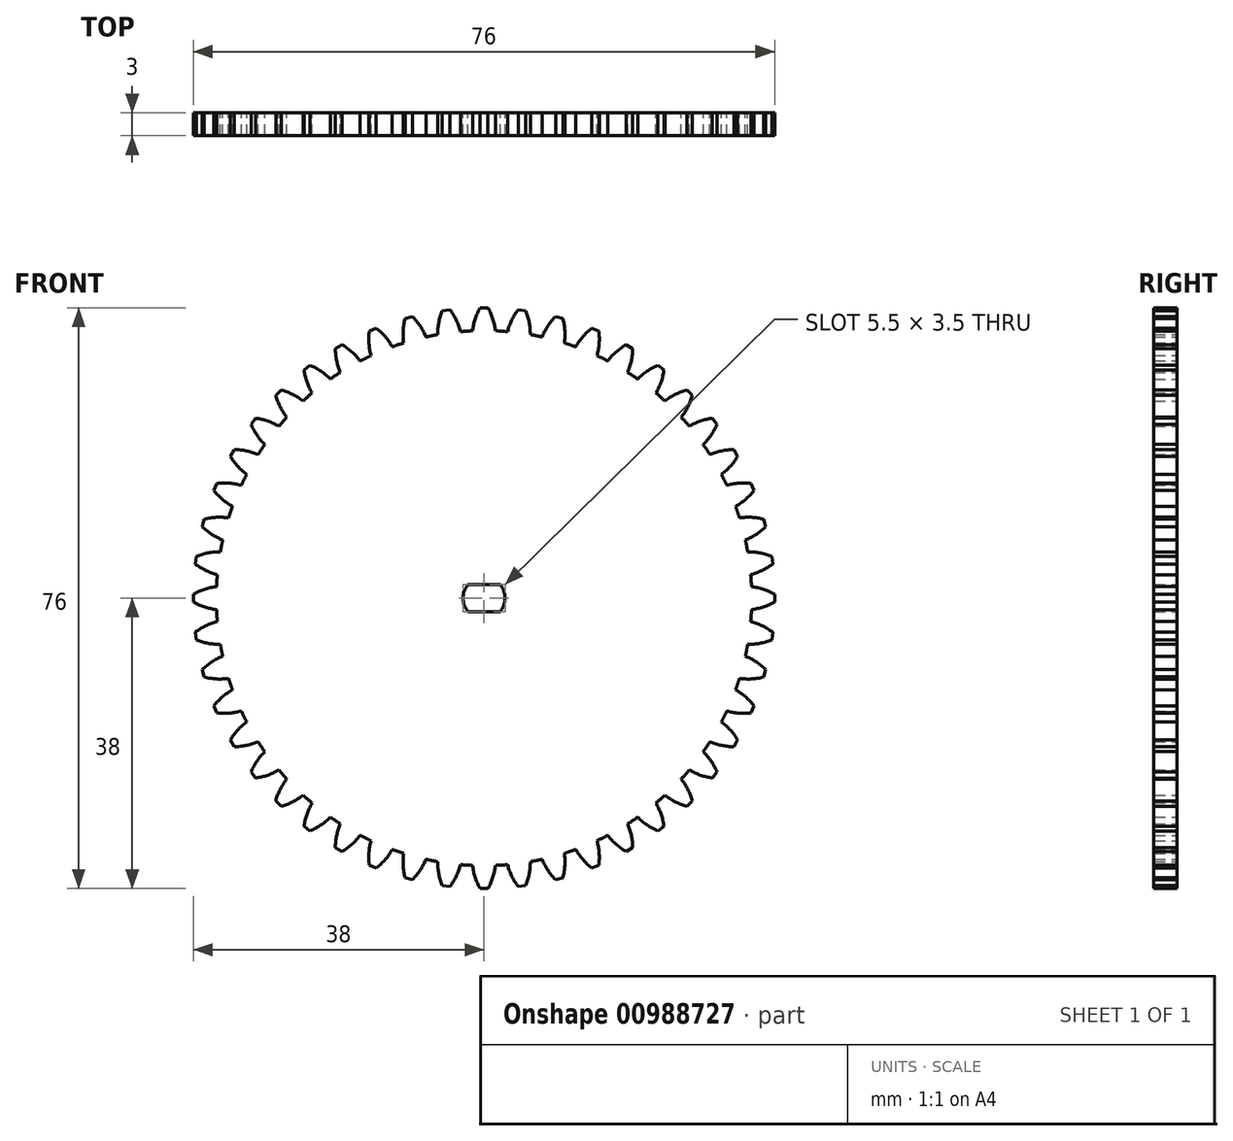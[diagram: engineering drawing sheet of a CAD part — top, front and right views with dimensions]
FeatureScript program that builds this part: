
annotation { "Feature Type Name" : "Feature", "Feature Type Description" : "" }
export const myFeature = defineFeature(function(context is Context, id is Id, definition is map)
    precondition{}
    {
        {
            var Q0;
            Q0=qCreatedBy(makeId("Front.planeOp"),FACE);
            var sketch = newSketch(context, id + "F0", { "sketchPlane" : qUnion([Q0])});
            skCircle(sketch, "E0", {"center": v(0, 0) * mm, "radius": 35 * mm});
            skLineSegment(sketch, "E1", {"start": v(-0.5, 38) * mm, "end": v(0.5, 38) * mm});
            skArc(sketch, "E2", {"start": v(-0.5, 38) * mm, "mid": v(-1.15, 36.53) * mm, "end": v(-1.5, 34.97) * mm});
            skArc(sketch, "E3", {"start": v(1.5, 34.97) * mm, "mid": v(1.15, 36.53) * mm, "end": v(0.5, 38) * mm});
            skLineSegment(sketch, "E4", {"start": v(0, 35) * mm, "end": v(0, 38) * mm, "construction": true});
            skLineSegment(sketch, "E5.1.0", {"start": v(-5.46, 37.6) * mm, "end": v(-4.46, 37.74) * mm});
            skArc(sketch, "E5.1.1", {"start": v(-5.46, 37.6) * mm, "mid": v(-5.91, 36.07) * mm, "end": v(-6.05, 34.47) * mm});
            skArc(sketch, "E5.1.2", {"start": v(-3.08, 34.86) * mm, "mid": v(-3.63, 36.37) * mm, "end": v(-4.46, 37.74) * mm});
            skLineSegment(sketch, "E5.2.0", {"start": v(-10.32, 36.58) * mm, "end": v(-9.35, 36.83) * mm});
            skArc(sketch, "E5.2.1", {"start": v(-10.32, 36.58) * mm, "mid": v(-10.57, 35) * mm, "end": v(-10.5, 33.39) * mm});
            skArc(sketch, "E5.2.2", {"start": v(-7.6, 34.16) * mm, "mid": v(-8.34, 35.59) * mm, "end": v(-9.35, 36.83) * mm});
            skLineSegment(sketch, "E5.3.0", {"start": v(-15, 34.92) * mm, "end": v(-14.08, 35.3) * mm});
            skArc(sketch, "E5.3.1", {"start": v(-15, 34.92) * mm, "mid": v(-15.05, 33.31) * mm, "end": v(-14.77, 31.73) * mm});
            skArc(sketch, "E5.3.2", {"start": v(-12, 32.88) * mm, "mid": v(-12.92, 34.2) * mm, "end": v(-14.08, 35.3) * mm});
            skLineSegment(sketch, "E5.4.0", {"start": v(-19.43, 32.66) * mm, "end": v(-18.57, 33.16) * mm});
            skArc(sketch, "E5.4.1", {"start": v(-19.43, 32.66) * mm, "mid": v(-19.27, 31.06) * mm, "end": v(-18.78, 29.53) * mm});
            skArc(sketch, "E5.4.2", {"start": v(-16.18, 31.03) * mm, "mid": v(-17.27, 32.22) * mm, "end": v(-18.57, 33.16) * mm});
            skLineSegment(sketch, "E5.5.0", {"start": v(-23.53, 29.84) * mm, "end": v(-22.74, 30.45) * mm});
            skArc(sketch, "E5.5.1", {"start": v(-23.53, 29.84) * mm, "mid": v(-23.16, 28.28) * mm, "end": v(-22.48, 26.83) * mm});
            skArc(sketch, "E5.5.2", {"start": v(-20.1, 28.65) * mm, "mid": v(-21.33, 29.69) * mm, "end": v(-22.74, 30.45) * mm});
            skLineSegment(sketch, "E5.6.0", {"start": v(-27.22, 26.52) * mm, "end": v(-26.52, 27.22) * mm});
            skArc(sketch, "E5.6.1", {"start": v(-27.22, 26.52) * mm, "mid": v(-26.65, 25.02) * mm, "end": v(-25.79, 23.67) * mm});
            skArc(sketch, "E5.6.2", {"start": v(-23.67, 25.79) * mm, "mid": v(-25.02, 26.65) * mm, "end": v(-26.52, 27.22) * mm});
            skLineSegment(sketch, "E5.7.0", {"start": v(-30.45, 22.74) * mm, "end": v(-29.84, 23.53) * mm});
            skArc(sketch, "E5.7.1", {"start": v(-30.45, 22.74) * mm, "mid": v(-29.69, 21.33) * mm, "end": v(-28.65, 20.1) * mm});
            skArc(sketch, "E5.7.2", {"start": v(-26.83, 22.48) * mm, "mid": v(-28.28, 23.16) * mm, "end": v(-29.84, 23.53) * mm});
            skLineSegment(sketch, "E5.8.0", {"start": v(-33.16, 18.57) * mm, "end": v(-32.66, 19.43) * mm});
            skArc(sketch, "E5.8.1", {"start": v(-33.16, 18.57) * mm, "mid": v(-32.22, 17.27) * mm, "end": v(-31.03, 16.18) * mm});
            skArc(sketch, "E5.8.2", {"start": v(-29.53, 18.78) * mm, "mid": v(-31.06, 19.27) * mm, "end": v(-32.66, 19.43) * mm});
            skLineSegment(sketch, "E5.9.0", {"start": v(-35.3, 14.08) * mm, "end": v(-34.92, 15) * mm});
            skArc(sketch, "E5.9.1", {"start": v(-35.3, 14.08) * mm, "mid": v(-34.2, 12.92) * mm, "end": v(-32.88, 12) * mm});
            skArc(sketch, "E5.9.2", {"start": v(-31.73, 14.77) * mm, "mid": v(-33.31, 15.05) * mm, "end": v(-34.92, 15) * mm});
            skLineSegment(sketch, "E5.10.0", {"start": v(-36.83, 9.35) * mm, "end": v(-36.58, 10.32) * mm});
            skArc(sketch, "E5.10.1", {"start": v(-36.83, 9.35) * mm, "mid": v(-35.59, 8.34) * mm, "end": v(-34.16, 7.6) * mm});
            skArc(sketch, "E5.10.2", {"start": v(-33.39, 10.5) * mm, "mid": v(-35, 10.57) * mm, "end": v(-36.58, 10.32) * mm});
            skLineSegment(sketch, "E5.11.0", {"start": v(-37.74, 4.46) * mm, "end": v(-37.6, 5.46) * mm});
            skArc(sketch, "E5.11.1", {"start": v(-37.74, 4.46) * mm, "mid": v(-36.37, 3.63) * mm, "end": v(-34.86, 3.08) * mm});
            skArc(sketch, "E5.11.2", {"start": v(-34.47, 6.05) * mm, "mid": v(-36.07, 5.91) * mm, "end": v(-37.6, 5.46) * mm});
            skLineSegment(sketch, "E5.12.0", {"start": v(-38, -0.5) * mm, "end": v(-38, 0.5) * mm});
            skArc(sketch, "E5.12.1", {"start": v(-38, -0.5) * mm, "mid": v(-36.53, -1.15) * mm, "end": v(-34.97, -1.5) * mm});
            skArc(sketch, "E5.12.2", {"start": v(-34.97, 1.5) * mm, "mid": v(-36.53, 1.15) * mm, "end": v(-38, 0.5) * mm});
            skLineSegment(sketch, "E5.13.0", {"start": v(-37.6, -5.46) * mm, "end": v(-37.74, -4.46) * mm});
            skArc(sketch, "E5.13.1", {"start": v(-37.6, -5.46) * mm, "mid": v(-36.07, -5.91) * mm, "end": v(-34.47, -6.05) * mm});
            skArc(sketch, "E5.13.2", {"start": v(-34.86, -3.08) * mm, "mid": v(-36.37, -3.63) * mm, "end": v(-37.74, -4.46) * mm});
            skLineSegment(sketch, "E5.14.0", {"start": v(-36.58, -10.32) * mm, "end": v(-36.83, -9.35) * mm});
            skArc(sketch, "E5.14.1", {"start": v(-36.58, -10.32) * mm, "mid": v(-35, -10.57) * mm, "end": v(-33.39, -10.5) * mm});
            skArc(sketch, "E5.14.2", {"start": v(-34.16, -7.6) * mm, "mid": v(-35.59, -8.34) * mm, "end": v(-36.83, -9.35) * mm});
            skLineSegment(sketch, "E5.15.0", {"start": v(-34.92, -15) * mm, "end": v(-35.3, -14.08) * mm});
            skArc(sketch, "E5.15.1", {"start": v(-34.92, -15) * mm, "mid": v(-33.31, -15.05) * mm, "end": v(-31.73, -14.77) * mm});
            skArc(sketch, "E5.15.2", {"start": v(-32.88, -12) * mm, "mid": v(-34.2, -12.92) * mm, "end": v(-35.3, -14.08) * mm});
            skLineSegment(sketch, "E5.16.0", {"start": v(-32.66, -19.43) * mm, "end": v(-33.16, -18.57) * mm});
            skArc(sketch, "E5.16.1", {"start": v(-32.66, -19.43) * mm, "mid": v(-31.06, -19.27) * mm, "end": v(-29.53, -18.78) * mm});
            skArc(sketch, "E5.16.2", {"start": v(-31.03, -16.18) * mm, "mid": v(-32.22, -17.27) * mm, "end": v(-33.16, -18.57) * mm});
            skLineSegment(sketch, "E5.17.0", {"start": v(-29.84, -23.53) * mm, "end": v(-30.45, -22.74) * mm});
            skArc(sketch, "E5.17.1", {"start": v(-29.84, -23.53) * mm, "mid": v(-28.28, -23.16) * mm, "end": v(-26.83, -22.48) * mm});
            skArc(sketch, "E5.17.2", {"start": v(-28.65, -20.1) * mm, "mid": v(-29.69, -21.33) * mm, "end": v(-30.45, -22.74) * mm});
            skLineSegment(sketch, "E5.18.0", {"start": v(-26.52, -27.22) * mm, "end": v(-27.22, -26.52) * mm});
            skArc(sketch, "E5.18.1", {"start": v(-26.52, -27.22) * mm, "mid": v(-25.02, -26.65) * mm, "end": v(-23.67, -25.79) * mm});
            skArc(sketch, "E5.18.2", {"start": v(-25.79, -23.67) * mm, "mid": v(-26.65, -25.02) * mm, "end": v(-27.22, -26.52) * mm});
            skLineSegment(sketch, "E5.19.0", {"start": v(-22.74, -30.45) * mm, "end": v(-23.53, -29.84) * mm});
            skArc(sketch, "E5.19.1", {"start": v(-22.74, -30.45) * mm, "mid": v(-21.33, -29.69) * mm, "end": v(-20.1, -28.65) * mm});
            skArc(sketch, "E5.19.2", {"start": v(-22.48, -26.83) * mm, "mid": v(-23.16, -28.28) * mm, "end": v(-23.53, -29.84) * mm});
            skLineSegment(sketch, "E5.20.0", {"start": v(-18.57, -33.16) * mm, "end": v(-19.43, -32.66) * mm});
            skArc(sketch, "E5.20.1", {"start": v(-18.57, -33.16) * mm, "mid": v(-17.27, -32.22) * mm, "end": v(-16.18, -31.03) * mm});
            skArc(sketch, "E5.20.2", {"start": v(-18.78, -29.53) * mm, "mid": v(-19.27, -31.06) * mm, "end": v(-19.43, -32.66) * mm});
            skLineSegment(sketch, "E5.21.0", {"start": v(-14.08, -35.3) * mm, "end": v(-15, -34.92) * mm});
            skArc(sketch, "E5.21.1", {"start": v(-14.08, -35.3) * mm, "mid": v(-12.92, -34.2) * mm, "end": v(-12, -32.88) * mm});
            skArc(sketch, "E5.21.2", {"start": v(-14.77, -31.73) * mm, "mid": v(-15.05, -33.31) * mm, "end": v(-15, -34.92) * mm});
            skLineSegment(sketch, "E5.22.0", {"start": v(-9.35, -36.83) * mm, "end": v(-10.32, -36.58) * mm});
            skArc(sketch, "E5.22.1", {"start": v(-9.35, -36.83) * mm, "mid": v(-8.34, -35.59) * mm, "end": v(-7.6, -34.16) * mm});
            skArc(sketch, "E5.22.2", {"start": v(-10.5, -33.39) * mm, "mid": v(-10.57, -35) * mm, "end": v(-10.32, -36.58) * mm});
            skLineSegment(sketch, "E5.23.0", {"start": v(-4.46, -37.74) * mm, "end": v(-5.46, -37.6) * mm});
            skArc(sketch, "E5.23.1", {"start": v(-4.46, -37.74) * mm, "mid": v(-3.63, -36.37) * mm, "end": v(-3.08, -34.86) * mm});
            skArc(sketch, "E5.23.2", {"start": v(-6.05, -34.47) * mm, "mid": v(-5.91, -36.07) * mm, "end": v(-5.46, -37.6) * mm});
            skLineSegment(sketch, "E5.24.0", {"start": v(0.5, -38) * mm, "end": v(-0.5, -38) * mm});
            skArc(sketch, "E5.24.1", {"start": v(0.5, -38) * mm, "mid": v(1.15, -36.53) * mm, "end": v(1.5, -34.97) * mm});
            skArc(sketch, "E5.24.2", {"start": v(-1.5, -34.97) * mm, "mid": v(-1.15, -36.53) * mm, "end": v(-0.5, -38) * mm});
            skLineSegment(sketch, "E5.25.0", {"start": v(5.46, -37.6) * mm, "end": v(4.46, -37.74) * mm});
            skArc(sketch, "E5.25.1", {"start": v(5.46, -37.6) * mm, "mid": v(5.91, -36.07) * mm, "end": v(6.05, -34.47) * mm});
            skArc(sketch, "E5.25.2", {"start": v(3.08, -34.86) * mm, "mid": v(3.63, -36.37) * mm, "end": v(4.46, -37.74) * mm});
            skLineSegment(sketch, "E5.26.0", {"start": v(10.32, -36.58) * mm, "end": v(9.35, -36.83) * mm});
            skArc(sketch, "E5.26.1", {"start": v(10.32, -36.58) * mm, "mid": v(10.57, -35) * mm, "end": v(10.5, -33.39) * mm});
            skArc(sketch, "E5.26.2", {"start": v(7.6, -34.16) * mm, "mid": v(8.34, -35.59) * mm, "end": v(9.35, -36.83) * mm});
            skLineSegment(sketch, "E5.27.0", {"start": v(15, -34.92) * mm, "end": v(14.08, -35.3) * mm});
            skArc(sketch, "E5.27.1", {"start": v(15, -34.92) * mm, "mid": v(15.05, -33.31) * mm, "end": v(14.77, -31.73) * mm});
            skArc(sketch, "E5.27.2", {"start": v(12, -32.88) * mm, "mid": v(12.92, -34.2) * mm, "end": v(14.08, -35.3) * mm});
            skLineSegment(sketch, "E5.28.0", {"start": v(19.43, -32.66) * mm, "end": v(18.57, -33.16) * mm});
            skArc(sketch, "E5.28.1", {"start": v(19.43, -32.66) * mm, "mid": v(19.27, -31.06) * mm, "end": v(18.78, -29.53) * mm});
            skArc(sketch, "E5.28.2", {"start": v(16.18, -31.03) * mm, "mid": v(17.27, -32.22) * mm, "end": v(18.57, -33.16) * mm});
            skLineSegment(sketch, "E5.29.0", {"start": v(23.53, -29.84) * mm, "end": v(22.74, -30.45) * mm});
            skArc(sketch, "E5.29.1", {"start": v(23.53, -29.84) * mm, "mid": v(23.16, -28.28) * mm, "end": v(22.48, -26.83) * mm});
            skArc(sketch, "E5.29.2", {"start": v(20.1, -28.65) * mm, "mid": v(21.33, -29.69) * mm, "end": v(22.74, -30.45) * mm});
            skLineSegment(sketch, "E5.30.0", {"start": v(27.22, -26.52) * mm, "end": v(26.52, -27.22) * mm});
            skArc(sketch, "E5.30.1", {"start": v(27.22, -26.52) * mm, "mid": v(26.65, -25.02) * mm, "end": v(25.79, -23.67) * mm});
            skArc(sketch, "E5.30.2", {"start": v(23.67, -25.79) * mm, "mid": v(25.02, -26.65) * mm, "end": v(26.52, -27.22) * mm});
            skLineSegment(sketch, "E5.31.0", {"start": v(30.45, -22.74) * mm, "end": v(29.84, -23.53) * mm});
            skArc(sketch, "E5.31.1", {"start": v(30.45, -22.74) * mm, "mid": v(29.69, -21.33) * mm, "end": v(28.65, -20.1) * mm});
            skArc(sketch, "E5.31.2", {"start": v(26.83, -22.48) * mm, "mid": v(28.28, -23.16) * mm, "end": v(29.84, -23.53) * mm});
            skLineSegment(sketch, "E5.32.0", {"start": v(33.16, -18.57) * mm, "end": v(32.66, -19.43) * mm});
            skArc(sketch, "E5.32.1", {"start": v(33.16, -18.57) * mm, "mid": v(32.22, -17.27) * mm, "end": v(31.03, -16.18) * mm});
            skArc(sketch, "E5.32.2", {"start": v(29.53, -18.78) * mm, "mid": v(31.06, -19.27) * mm, "end": v(32.66, -19.43) * mm});
            skLineSegment(sketch, "E5.33.0", {"start": v(35.3, -14.08) * mm, "end": v(34.92, -15) * mm});
            skArc(sketch, "E5.33.1", {"start": v(35.3, -14.08) * mm, "mid": v(34.2, -12.92) * mm, "end": v(32.88, -12) * mm});
            skArc(sketch, "E5.33.2", {"start": v(31.73, -14.77) * mm, "mid": v(33.31, -15.05) * mm, "end": v(34.92, -15) * mm});
            skLineSegment(sketch, "E5.34.0", {"start": v(36.83, -9.35) * mm, "end": v(36.58, -10.32) * mm});
            skArc(sketch, "E5.34.1", {"start": v(36.83, -9.35) * mm, "mid": v(35.59, -8.34) * mm, "end": v(34.16, -7.6) * mm});
            skArc(sketch, "E5.34.2", {"start": v(33.39, -10.5) * mm, "mid": v(35, -10.57) * mm, "end": v(36.58, -10.32) * mm});
            skLineSegment(sketch, "E5.35.0", {"start": v(37.74, -4.46) * mm, "end": v(37.6, -5.46) * mm});
            skArc(sketch, "E5.35.1", {"start": v(37.74, -4.46) * mm, "mid": v(36.37, -3.63) * mm, "end": v(34.86, -3.08) * mm});
            skArc(sketch, "E5.35.2", {"start": v(34.47, -6.05) * mm, "mid": v(36.07, -5.91) * mm, "end": v(37.6, -5.46) * mm});
            skLineSegment(sketch, "E5.36.0", {"start": v(38, 0.5) * mm, "end": v(38, -0.5) * mm});
            skArc(sketch, "E5.36.1", {"start": v(38, 0.5) * mm, "mid": v(36.53, 1.15) * mm, "end": v(34.97, 1.5) * mm});
            skArc(sketch, "E5.36.2", {"start": v(34.97, -1.5) * mm, "mid": v(36.53, -1.15) * mm, "end": v(38, -0.5) * mm});
            skLineSegment(sketch, "E5.37.0", {"start": v(37.6, 5.46) * mm, "end": v(37.74, 4.46) * mm});
            skArc(sketch, "E5.37.1", {"start": v(37.6, 5.46) * mm, "mid": v(36.07, 5.91) * mm, "end": v(34.47, 6.05) * mm});
            skArc(sketch, "E5.37.2", {"start": v(34.86, 3.08) * mm, "mid": v(36.37, 3.63) * mm, "end": v(37.74, 4.46) * mm});
            skLineSegment(sketch, "E5.38.0", {"start": v(36.58, 10.32) * mm, "end": v(36.83, 9.35) * mm});
            skArc(sketch, "E5.38.1", {"start": v(36.58, 10.32) * mm, "mid": v(35, 10.57) * mm, "end": v(33.39, 10.5) * mm});
            skArc(sketch, "E5.38.2", {"start": v(34.16, 7.6) * mm, "mid": v(35.59, 8.34) * mm, "end": v(36.83, 9.35) * mm});
            skLineSegment(sketch, "E6.1.39.0", {"start": v(34.92, 15) * mm, "end": v(35.3, 14.08) * mm});
            skArc(sketch, "E6.3.39.0", {"start": v(34.92, 15) * mm, "mid": v(33.31, 15.05) * mm, "end": v(31.73, 14.77) * mm});
            skArc(sketch, "E6.7.39.0", {"start": v(32.88, 12) * mm, "mid": v(34.2, 12.92) * mm, "end": v(35.3, 14.08) * mm});
            skLineSegment(sketch, "E6.1.40.0", {"start": v(32.66, 19.43) * mm, "end": v(33.16, 18.57) * mm});
            skArc(sketch, "E6.3.40.0", {"start": v(32.66, 19.43) * mm, "mid": v(31.06, 19.27) * mm, "end": v(29.53, 18.78) * mm});
            skArc(sketch, "E6.7.40.0", {"start": v(31.03, 16.18) * mm, "mid": v(32.22, 17.27) * mm, "end": v(33.16, 18.57) * mm});
            skLineSegment(sketch, "E6.1.41.0", {"start": v(29.84, 23.53) * mm, "end": v(30.45, 22.74) * mm});
            skArc(sketch, "E6.3.41.0", {"start": v(29.84, 23.53) * mm, "mid": v(28.28, 23.16) * mm, "end": v(26.83, 22.48) * mm});
            skArc(sketch, "E6.7.41.0", {"start": v(28.65, 20.1) * mm, "mid": v(29.69, 21.33) * mm, "end": v(30.45, 22.74) * mm});
            skLineSegment(sketch, "E7.1.42.0", {"start": v(26.52, 27.22) * mm, "end": v(27.22, 26.52) * mm});
            skArc(sketch, "E7.3.42.0", {"start": v(26.52, 27.22) * mm, "mid": v(25.02, 26.65) * mm, "end": v(23.67, 25.79) * mm});
            skArc(sketch, "E7.7.42.0", {"start": v(25.79, 23.67) * mm, "mid": v(26.65, 25.02) * mm, "end": v(27.22, 26.52) * mm});
            skLineSegment(sketch, "E7.1.43.0", {"start": v(22.74, 30.45) * mm, "end": v(23.53, 29.84) * mm});
            skArc(sketch, "E7.3.43.0", {"start": v(22.74, 30.45) * mm, "mid": v(21.33, 29.69) * mm, "end": v(20.1, 28.65) * mm});
            skArc(sketch, "E7.7.43.0", {"start": v(22.48, 26.83) * mm, "mid": v(23.16, 28.28) * mm, "end": v(23.53, 29.84) * mm});
            skLineSegment(sketch, "E7.1.44.0", {"start": v(18.57, 33.16) * mm, "end": v(19.43, 32.66) * mm});
            skArc(sketch, "E7.3.44.0", {"start": v(18.57, 33.16) * mm, "mid": v(17.27, 32.22) * mm, "end": v(16.18, 31.03) * mm});
            skArc(sketch, "E7.7.44.0", {"start": v(18.78, 29.53) * mm, "mid": v(19.27, 31.06) * mm, "end": v(19.43, 32.66) * mm});
            skLineSegment(sketch, "E7.1.45.0", {"start": v(14.08, 35.3) * mm, "end": v(15, 34.92) * mm});
            skArc(sketch, "E7.3.45.0", {"start": v(14.08, 35.3) * mm, "mid": v(12.92, 34.2) * mm, "end": v(12, 32.88) * mm});
            skArc(sketch, "E7.7.45.0", {"start": v(14.77, 31.73) * mm, "mid": v(15.05, 33.31) * mm, "end": v(15, 34.92) * mm});
            skLineSegment(sketch, "E8.1.46.0", {"start": v(9.35, 36.83) * mm, "end": v(10.32, 36.58) * mm});
            skArc(sketch, "E8.3.46.0", {"start": v(9.35, 36.83) * mm, "mid": v(8.34, 35.59) * mm, "end": v(7.6, 34.16) * mm});
            skArc(sketch, "E8.7.46.0", {"start": v(10.5, 33.39) * mm, "mid": v(10.57, 35) * mm, "end": v(10.32, 36.58) * mm});
            skLineSegment(sketch, "E8.1.47.0", {"start": v(4.46, 37.74) * mm, "end": v(5.46, 37.6) * mm});
            skArc(sketch, "E8.3.47.0", {"start": v(4.46, 37.74) * mm, "mid": v(3.63, 36.37) * mm, "end": v(3.08, 34.86) * mm});
            skArc(sketch, "E8.7.47.0", {"start": v(6.05, 34.47) * mm, "mid": v(5.91, 36.07) * mm, "end": v(5.46, 37.6) * mm});
            skCircle(sketch, "E9", {"center": v(0, 0) * mm, "radius": 2.75 * mm});
            skLineSegment(sketch, "E10", {"start": v(-2.75, 0) * mm, "end": v(2.75, 0) * mm, "construction": true});
            skLineSegment(sketch, "E11", {"start": v(-2.12, 1.75) * mm, "end": v(2.12, 1.75) * mm});
            skLineSegment(sketch, "E12", {"start": v(-2.12, -1.75) * mm, "end": v(2.12, -1.75) * mm});
            skSolve(sketch);
        }
        {
            var Q0;
            {var subQ0=sQuery(id+"F0.wireOp",EDGE,"E0");var subQ69=makeQuery(id+"F0.imprint","INTERSECT",VERTEX,{"derivedFrom":[subQ0,sQuery(id+"F0.wireOp",EDGE,"E5.37.1")]});Q0=makeQuery(id+"F0.imprint","IMPRINT",FACE,{"disambiguationData":[TD([[makeQuery(id+"F0.imprint","IMPRINT",EDGE,{"disambiguationData":[TD([[subQ69,-1.0]])],"derivedFrom":subQ0}),1.0]])]});}
            var Q1;
            Q1=makeQuery(id+"F0.imprint","IMPRINT",FACE,{"disambiguationData":[TD([[makeQuery(id+"F0.imprint","IMPRINT",EDGE,{"derivedFrom":sQuery(id+"F0.wireOp",EDGE,"E5.9.0")}),-1.0]])]});
            var Q2;
            Q2=makeQuery(id+"F0.imprint","IMPRINT",FACE,{"disambiguationData":[TD([[makeQuery(id+"F0.imprint","IMPRINT",EDGE,{"derivedFrom":sQuery(id+"F0.wireOp",EDGE,"E5.8.0")}),-1.0]])]});
            var Q3;
            Q3=makeQuery(id+"F0.imprint","IMPRINT",FACE,{"disambiguationData":[TD([[makeQuery(id+"F0.imprint","IMPRINT",EDGE,{"derivedFrom":sQuery(id+"F0.wireOp",EDGE,"E5.7.0")}),-1.0]])]});
            var Q4;
            Q4=makeQuery(id+"F0.imprint","IMPRINT",FACE,{"disambiguationData":[TD([[makeQuery(id+"F0.imprint","IMPRINT",EDGE,{"derivedFrom":sQuery(id+"F0.wireOp",EDGE,"E5.6.0")}),-1.0]])]});
            var Q5;
            Q5=makeQuery(id+"F0.imprint","IMPRINT",FACE,{"disambiguationData":[TD([[makeQuery(id+"F0.imprint","IMPRINT",EDGE,{"derivedFrom":sQuery(id+"F0.wireOp",EDGE,"E5.5.0")}),-1.0]])]});
            var Q6;
            Q6=makeQuery(id+"F0.imprint","IMPRINT",FACE,{"disambiguationData":[TD([[makeQuery(id+"F0.imprint","IMPRINT",EDGE,{"derivedFrom":sQuery(id+"F0.wireOp",EDGE,"E5.4.0")}),-1.0]])]});
            var Q7;
            Q7=makeQuery(id+"F0.imprint","IMPRINT",FACE,{"disambiguationData":[TD([[makeQuery(id+"F0.imprint","IMPRINT",EDGE,{"derivedFrom":sQuery(id+"F0.wireOp",EDGE,"E5.1.0")}),-1.0]])]});
            var Q8;
            Q8=makeQuery(id+"F0.imprint","IMPRINT",FACE,{"disambiguationData":[TD([[makeQuery(id+"F0.imprint","IMPRINT",EDGE,{"derivedFrom":sQuery(id+"F0.wireOp",EDGE,"E1")}),-1.0]])]});
            var Q9;
            Q9=makeQuery(id+"F0.imprint","IMPRINT",FACE,{"disambiguationData":[TD([[makeQuery(id+"F0.imprint","IMPRINT",EDGE,{"derivedFrom":sQuery(id+"F0.wireOp",EDGE,"E5.2.0")}),-1.0]])]});
            var Q10;
            Q10=makeQuery(id+"F0.imprint","IMPRINT",FACE,{"disambiguationData":[TD([[makeQuery(id+"F0.imprint","IMPRINT",EDGE,{"derivedFrom":sQuery(id+"F0.wireOp",EDGE,"E5.3.0")}),-1.0]])]});
            var Q11;
            Q11=makeQuery(id+"F0.imprint","IMPRINT",FACE,{"disambiguationData":[TD([[makeQuery(id+"F0.imprint","IMPRINT",EDGE,{"derivedFrom":sQuery(id+"F0.wireOp",EDGE,"E8.1.48.0")}),-1.0]])]});
            var Q12;
            Q12=makeQuery(id+"F0.imprint","IMPRINT",FACE,{"disambiguationData":[TD([[makeQuery(id+"F0.imprint","IMPRINT",EDGE,{"derivedFrom":sQuery(id+"F0.wireOp",EDGE,"E8.1.47.0")}),-1.0]])]});
            var Q13;
            Q13=makeQuery(id+"F0.imprint","IMPRINT",FACE,{"disambiguationData":[TD([[makeQuery(id+"F0.imprint","IMPRINT",EDGE,{"derivedFrom":sQuery(id+"F0.wireOp",EDGE,"E8.1.46.0")}),-1.0]])]});
            var Q14;
            Q14=makeQuery(id+"F0.imprint","IMPRINT",FACE,{"disambiguationData":[TD([[makeQuery(id+"F0.imprint","IMPRINT",EDGE,{"derivedFrom":sQuery(id+"F0.wireOp",EDGE,"E7.1.45.0")}),-1.0]])]});
            var Q15;
            Q15=makeQuery(id+"F0.imprint","IMPRINT",FACE,{"disambiguationData":[TD([[makeQuery(id+"F0.imprint","IMPRINT",EDGE,{"derivedFrom":sQuery(id+"F0.wireOp",EDGE,"E7.1.44.0")}),-1.0]])]});
            var Q16;
            Q16=makeQuery(id+"F0.imprint","IMPRINT",FACE,{"disambiguationData":[TD([[makeQuery(id+"F0.imprint","IMPRINT",EDGE,{"derivedFrom":sQuery(id+"F0.wireOp",EDGE,"E7.1.43.0")}),-1.0]])]});
            var Q17;
            Q17=makeQuery(id+"F0.imprint","IMPRINT",FACE,{"disambiguationData":[TD([[makeQuery(id+"F0.imprint","IMPRINT",EDGE,{"derivedFrom":sQuery(id+"F0.wireOp",EDGE,"E7.1.42.0")}),-1.0]])]});
            var Q18;
            Q18=makeQuery(id+"F0.imprint","IMPRINT",FACE,{"disambiguationData":[TD([[makeQuery(id+"F0.imprint","IMPRINT",EDGE,{"derivedFrom":sQuery(id+"F0.wireOp",EDGE,"E6.1.41.0")}),-1.0]])]});
            var Q19;
            Q19=makeQuery(id+"F0.imprint","IMPRINT",FACE,{"disambiguationData":[TD([[makeQuery(id+"F0.imprint","IMPRINT",EDGE,{"derivedFrom":sQuery(id+"F0.wireOp",EDGE,"E6.1.40.0")}),-1.0]])]});
            var Q20;
            Q20=makeQuery(id+"F0.imprint","IMPRINT",FACE,{"disambiguationData":[TD([[makeQuery(id+"F0.imprint","IMPRINT",EDGE,{"derivedFrom":sQuery(id+"F0.wireOp",EDGE,"E6.1.39.0")}),-1.0]])]});
            var Q21;
            Q21=makeQuery(id+"F0.imprint","IMPRINT",FACE,{"disambiguationData":[TD([[makeQuery(id+"F0.imprint","IMPRINT",EDGE,{"derivedFrom":sQuery(id+"F0.wireOp",EDGE,"E5.38.0")}),-1.0]])]});
            var Q22;
            Q22=makeQuery(id+"F0.imprint","IMPRINT",FACE,{"disambiguationData":[TD([[makeQuery(id+"F0.imprint","IMPRINT",EDGE,{"derivedFrom":sQuery(id+"F0.wireOp",EDGE,"E5.37.0")}),-1.0]])]});
            var Q23;
            Q23=makeQuery(id+"F0.imprint","IMPRINT",FACE,{"disambiguationData":[TD([[makeQuery(id+"F0.imprint","IMPRINT",EDGE,{"derivedFrom":sQuery(id+"F0.wireOp",EDGE,"E5.36.0")}),-1.0]])]});
            var Q24;
            Q24=makeQuery(id+"F0.imprint","IMPRINT",FACE,{"disambiguationData":[TD([[makeQuery(id+"F0.imprint","IMPRINT",EDGE,{"derivedFrom":sQuery(id+"F0.wireOp",EDGE,"E5.35.0")}),-1.0]])]});
            var Q25;
            Q25=makeQuery(id+"F0.imprint","IMPRINT",FACE,{"disambiguationData":[TD([[makeQuery(id+"F0.imprint","IMPRINT",EDGE,{"derivedFrom":sQuery(id+"F0.wireOp",EDGE,"E5.34.0")}),-1.0]])]});
            var Q26;
            Q26=makeQuery(id+"F0.imprint","IMPRINT",FACE,{"disambiguationData":[TD([[makeQuery(id+"F0.imprint","IMPRINT",EDGE,{"derivedFrom":sQuery(id+"F0.wireOp",EDGE,"E5.33.0")}),-1.0]])]});
            var Q27;
            Q27=makeQuery(id+"F0.imprint","IMPRINT",FACE,{"disambiguationData":[TD([[makeQuery(id+"F0.imprint","IMPRINT",EDGE,{"derivedFrom":sQuery(id+"F0.wireOp",EDGE,"E5.32.0")}),-1.0]])]});
            var Q28;
            Q28=makeQuery(id+"F0.imprint","IMPRINT",FACE,{"disambiguationData":[TD([[makeQuery(id+"F0.imprint","IMPRINT",EDGE,{"derivedFrom":sQuery(id+"F0.wireOp",EDGE,"E5.31.0")}),-1.0]])]});
            var Q29;
            Q29=makeQuery(id+"F0.imprint","IMPRINT",FACE,{"disambiguationData":[TD([[makeQuery(id+"F0.imprint","IMPRINT",EDGE,{"derivedFrom":sQuery(id+"F0.wireOp",EDGE,"E5.30.0")}),-1.0]])]});
            var Q30;
            Q30=makeQuery(id+"F0.imprint","IMPRINT",FACE,{"disambiguationData":[TD([[makeQuery(id+"F0.imprint","IMPRINT",EDGE,{"derivedFrom":sQuery(id+"F0.wireOp",EDGE,"E5.29.0")}),-1.0]])]});
            var Q31;
            Q31=makeQuery(id+"F0.imprint","IMPRINT",FACE,{"disambiguationData":[TD([[makeQuery(id+"F0.imprint","IMPRINT",EDGE,{"derivedFrom":sQuery(id+"F0.wireOp",EDGE,"E5.28.0")}),-1.0]])]});
            var Q32;
            Q32=makeQuery(id+"F0.imprint","IMPRINT",FACE,{"disambiguationData":[TD([[makeQuery(id+"F0.imprint","IMPRINT",EDGE,{"derivedFrom":sQuery(id+"F0.wireOp",EDGE,"E5.27.0")}),-1.0]])]});
            var Q33;
            Q33=makeQuery(id+"F0.imprint","IMPRINT",FACE,{"disambiguationData":[TD([[makeQuery(id+"F0.imprint","IMPRINT",EDGE,{"derivedFrom":sQuery(id+"F0.wireOp",EDGE,"E5.26.0")}),-1.0]])]});
            var Q34;
            Q34=makeQuery(id+"F0.imprint","IMPRINT",FACE,{"disambiguationData":[TD([[makeQuery(id+"F0.imprint","IMPRINT",EDGE,{"derivedFrom":sQuery(id+"F0.wireOp",EDGE,"E5.25.0")}),-1.0]])]});
            var Q35;
            Q35=makeQuery(id+"F0.imprint","IMPRINT",FACE,{"disambiguationData":[TD([[makeQuery(id+"F0.imprint","IMPRINT",EDGE,{"derivedFrom":sQuery(id+"F0.wireOp",EDGE,"E5.24.0")}),-1.0]])]});
            var Q36;
            Q36=makeQuery(id+"F0.imprint","IMPRINT",FACE,{"disambiguationData":[TD([[makeQuery(id+"F0.imprint","IMPRINT",EDGE,{"derivedFrom":sQuery(id+"F0.wireOp",EDGE,"E5.23.0")}),-1.0]])]});
            var Q37;
            Q37=makeQuery(id+"F0.imprint","IMPRINT",FACE,{"disambiguationData":[TD([[makeQuery(id+"F0.imprint","IMPRINT",EDGE,{"derivedFrom":sQuery(id+"F0.wireOp",EDGE,"E5.22.0")}),-1.0]])]});
            var Q38;
            Q38=makeQuery(id+"F0.imprint","IMPRINT",FACE,{"disambiguationData":[TD([[makeQuery(id+"F0.imprint","IMPRINT",EDGE,{"derivedFrom":sQuery(id+"F0.wireOp",EDGE,"E5.21.0")}),-1.0]])]});
            var Q39;
            Q39=makeQuery(id+"F0.imprint","IMPRINT",FACE,{"disambiguationData":[TD([[makeQuery(id+"F0.imprint","IMPRINT",EDGE,{"derivedFrom":sQuery(id+"F0.wireOp",EDGE,"E5.20.0")}),-1.0]])]});
            var Q40;
            Q40=makeQuery(id+"F0.imprint","IMPRINT",FACE,{"disambiguationData":[TD([[makeQuery(id+"F0.imprint","IMPRINT",EDGE,{"derivedFrom":sQuery(id+"F0.wireOp",EDGE,"E5.19.0")}),-1.0]])]});
            var Q41;
            Q41=makeQuery(id+"F0.imprint","IMPRINT",FACE,{"disambiguationData":[TD([[makeQuery(id+"F0.imprint","IMPRINT",EDGE,{"derivedFrom":sQuery(id+"F0.wireOp",EDGE,"E5.18.0")}),-1.0]])]});
            var Q42;
            Q42=makeQuery(id+"F0.imprint","IMPRINT",FACE,{"disambiguationData":[TD([[makeQuery(id+"F0.imprint","IMPRINT",EDGE,{"derivedFrom":sQuery(id+"F0.wireOp",EDGE,"E5.17.0")}),-1.0]])]});
            var Q43;
            Q43=makeQuery(id+"F0.imprint","IMPRINT",FACE,{"disambiguationData":[TD([[makeQuery(id+"F0.imprint","IMPRINT",EDGE,{"derivedFrom":sQuery(id+"F0.wireOp",EDGE,"E5.16.0")}),-1.0]])]});
            var Q44;
            Q44=makeQuery(id+"F0.imprint","IMPRINT",FACE,{"disambiguationData":[TD([[makeQuery(id+"F0.imprint","IMPRINT",EDGE,{"derivedFrom":sQuery(id+"F0.wireOp",EDGE,"E5.15.0")}),-1.0]])]});
            var Q45;
            Q45=makeQuery(id+"F0.imprint","IMPRINT",FACE,{"disambiguationData":[TD([[makeQuery(id+"F0.imprint","IMPRINT",EDGE,{"derivedFrom":sQuery(id+"F0.wireOp",EDGE,"E5.14.0")}),-1.0]])]});
            var Q46;
            Q46=makeQuery(id+"F0.imprint","IMPRINT",FACE,{"disambiguationData":[TD([[makeQuery(id+"F0.imprint","IMPRINT",EDGE,{"derivedFrom":sQuery(id+"F0.wireOp",EDGE,"E5.13.0")}),-1.0]])]});
            var Q47;
            Q47=makeQuery(id+"F0.imprint","IMPRINT",FACE,{"disambiguationData":[TD([[makeQuery(id+"F0.imprint","IMPRINT",EDGE,{"derivedFrom":sQuery(id+"F0.wireOp",EDGE,"E5.12.0")}),-1.0]])]});
            var Q48;
            Q48=makeQuery(id+"F0.imprint","IMPRINT",FACE,{"disambiguationData":[TD([[makeQuery(id+"F0.imprint","IMPRINT",EDGE,{"derivedFrom":sQuery(id+"F0.wireOp",EDGE,"E5.11.0")}),-1.0]])]});
            var Q49;
            Q49=makeQuery(id+"F0.imprint","IMPRINT",FACE,{"disambiguationData":[TD([[makeQuery(id+"F0.imprint","IMPRINT",EDGE,{"derivedFrom":sQuery(id+"F0.wireOp",EDGE,"E5.10.0")}),-1.0]])]});
            var Q50;
            {var subQ0=sQuery(id+"F0.wireOp",EDGE,"E11");Q50=makeQuery(id+"F0.imprint","IMPRINT",FACE,{"disambiguationData":[TD([[makeQuery(id+"F0.imprint","IMPRINT",EDGE,{"derivedFrom":subQ0}),1.0]])]});}
            var Q51;
            {var subQ0=sQuery(id+"F0.wireOp",EDGE,"E12");Q51=makeQuery(id+"F0.imprint","IMPRINT",FACE,{"disambiguationData":[TD([[makeQuery(id+"F0.imprint","IMPRINT",EDGE,{"derivedFrom":subQ0}),-1.0]])]});}
            extrude(context, id + "F1", {"entities" : qUnion([Q0, Q1, Q2, Q3, Q4, Q5, Q6, Q7, Q8, Q9, Q10, Q11, Q12, Q13, Q14, Q15, Q16, Q17, Q18, Q19, Q20, Q21, Q22, Q23, Q24, Q25, Q26, Q27, Q28, Q29, Q30, Q31, Q32, Q33, Q34, Q35, Q36, Q37, Q38, Q39, Q40, Q41, Q42, Q43, Q44, Q45, Q46, Q47, Q48, Q49, Q50, Q51]), "depth" : 3 * mm, "offsetDistance" : 25 * mm});
        }
    });
